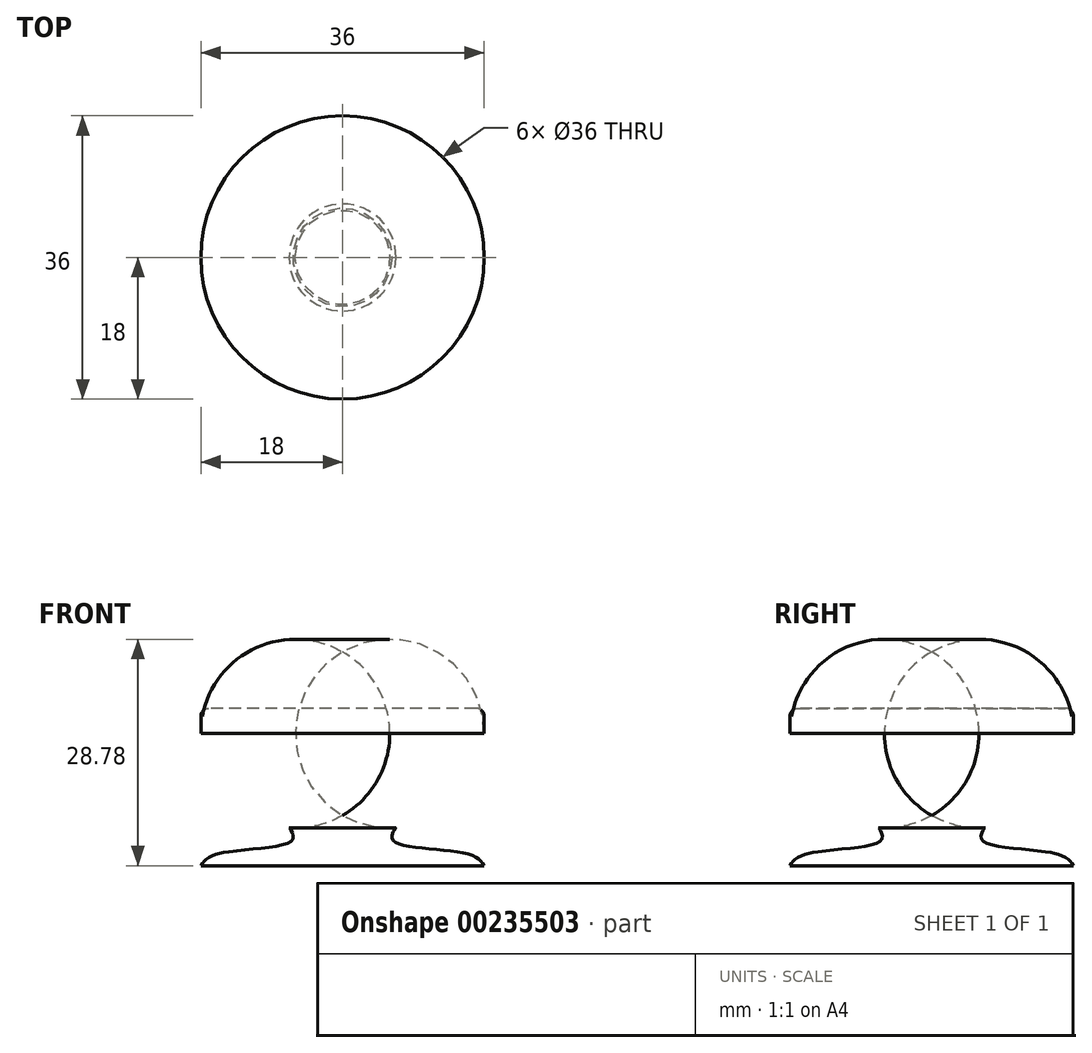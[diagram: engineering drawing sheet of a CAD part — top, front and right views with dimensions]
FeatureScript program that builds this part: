
annotation { "Feature Type Name" : "Feature", "Feature Type Description" : "" }
export const myFeature = defineFeature(function(context is Context, id is Id, definition is map)
    precondition{}
    {
        {
            var Q0;
            Q0=qCreatedBy(makeId("Front.planeOp"),FACE);
            var sketch = newSketch(context, id + "F0", { "sketchPlane" : qUnion([Q0])});
            skLineSegment(sketch, "E0", {"start": v(0, 0) * mm, "end": v(0, 170.02) * mm, "construction": true});
            skLineSegment(sketch, "E1", {"start": v(-44.09, 0) * mm, "end": v(109.88, 0) * mm, "construction": true});
            skLineSegment(sketch, "E2", {"start": v(-46.54, 70) * mm, "end": v(86.34, 70) * mm, "construction": true});
            skLineSegment(sketch, "E3", {"start": v(0, 20) * mm, "end": v(17, 20) * mm});
            skLineSegment(sketch, "E4", {"start": v(18, 19) * mm, "end": v(18, 16.78) * mm});
            skArc(sketch, "E5", {"start": v(6.8, 4.8) * mm, "mid": v(14.76, 8.58) * mm, "end": v(18, 16.78) * mm});
            skFitSpline(sketch, "E6", {"points": [v(6.75, 4.8) * mm, v(6.75, 2.97) * mm, v(15.78, 1.53) * mm, v(18, 0) * mm], "startDerivative": vector(-8.21, -11.8) * mm, "endDerivative": vector(4.41, -7.13) * mm});
            skLineSegment(sketch, "E7", {"start": v(18, 0) * mm, "end": v(0, 0) * mm});
            skArc(sketch, "E8.filletArc", {"start": v(6.8, 4.8) * mm, "mid": v(6.75, 4.8) * mm, "end": v(6.72, 4.76) * mm});
            skPoint(sketch, "E9.visualSharp", {"position": v(18, 20) * mm});
            skArc(sketch, "E9.filletArc", {"start": v(18, 19) * mm, "mid": v(17.7, 19.7) * mm, "end": v(17, 20) * mm});
            skLineSegment(sketch, "E10", {"start": v(0, 20) * mm, "end": v(0, 0) * mm});
            skSolve(sketch);
        }
        {
            var Q0;
            Q0=makeQuery(id+"F0.imprint","IMPRINT",FACE,{"disambiguationData":[TD([[makeQuery(id+"F0.imprint","IMPRINT",EDGE,{"derivedFrom":sQuery(id+"F0.wireOp",EDGE,"E3")}),-1.0]])]});
            var Q1;
            Q1=sQuery(id+"F0.wireOp",EDGE,"E10");
            revolve(context, id + "F1", {"entities" : qUnion([Q0]), "axis" : qUnion([Q1]), "revolveType" : RevolveType.FULL});
        }
    });
